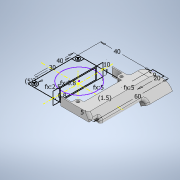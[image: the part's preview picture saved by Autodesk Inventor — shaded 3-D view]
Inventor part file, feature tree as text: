
AUTODESK INVENTOR PART (.ipt)
format: ipt  version: 2020.2 (Build 242310000, 310)  size: 784,384 bytes
history: native  units: mm
features: extrude x16, sketch x6, draft x6, thicken_offset x5, plane x4, fillet x3, projected_geometry x3, shell x1
ambient origin geometry x8: Origin, YZ Plane, XZ Plane, XY Plane, X Axis, Y Axis, Z Axis, Center Point
bodies: Solid1 (feature_tree), Solid3 (feature_tree)
feature tree (44):
  sketch  "Sketch2"  dims[d0=40.0mm d1=40.0mm]
  sketch  "Sketch15"  dims[d6=10.0mm d7=5.0mm]
  plane  "Work Plane1"
  sketch  "Sketch3"  dims[d2=2.5mm d3=30.0mm]
  sketch  "Sketch5"  dims[d4=5.0mm d5=3.0mm]
  plane  "Work Plane2"
  extrude  "Extrusion1"  Depth=40.0mm
  extrude  "Extrusion2"  Depth=30.0mm
  extrude  "Extrusion12"  Depth=3.0mm
  extrude  "Extrusion3"  Depth=10.0mm
  extrude  "Extrusion4"  TaperAngle=0.0deg  [1 undecoded]
  extrude  "Extrusion10"  Depth=10.0mm TaperAngle=0.0deg
  extrude  "Extrusion5"  Depth=10.0mm
  plane  "Work Plane4"
  plane  "Work Plane7"
  extrude  "Extrusion28"  TaperAngle=0.0deg  [1 undecoded]
  extrude  "Extrusion29"  Depth=10.0mm
  draft  "FaceDraft20"
  draft  "FaceDraft21"
  draft  "FaceDraft22"
  draft  "FaceDraft23"
  extrude  "Extrusion31"  Depth=10.0mm
  draft  "FaceDraft29"
  fillet  "Fillet28"  Radius=20.0mm
  shell  "Shell4"  Thickness=0.0mm
  extrude  "Extrusion33"  Depth=10.0mm
  extrude  "Extrusion34"  Depth=10.0mm
  extrude  "Extrusion39"  TaperAngle=0.0deg  [1 undecoded]
  extrude  "Extrusion35"  Depth=10.0mm
  draft  "FaceDraft30"
  extrude  "Extrusion37"  Depth=10.0mm
  extrude  "Extrusion36"  [1 undecoded]
  thicken_offset  "Thicken16"
  thicken_offset  "Thicken20"
  thicken_offset  "Thicken17"
  fillet  "Fillet26"  Radius=20.0mm
  fillet  "Fillet22"  Radius=0.5mm
  thicken_offset  "Thicken18"
  thicken_offset  "Thicken19"
  sketch  "Sketch18"  dims[d8=1.4mm d9=0.0mm]
  projected_geometry  "Projected Loop4"
  sketch  "Sketch19"  dims[d10=0.0mm d11=1.4mm d12=0.0mm d13=5.0mm d14=0.0mm d15=0.8mm d16=0.8mm d17=20.0mm d18=0.0mm d19=20.0mm d25=5.0mm d26=0.0mm d28=1.5mm d36=60.0mm d44=-5.0mm d69=20.0mm d71=0.5mm d72=0.0mm d76=5.0mm d77=0.0mm d112=9.0mm d121=12.0mm d122=0.0mm d126=-12.0mm d168=5.0mm d188=30.0deg d198=15.0mm d210=5.0mm d211=5.0mm d212=0.0mm d213=11.0mm d214=0.0mm d217=30.0deg d218=30.0deg d225=0.8mm d226=30.0deg d227=30.0deg d228=5.0mm d229=10.0mm d230=0.0mm d239=30.0deg d241=0.0mm d242=0.0mm d243=10.0mm d244=0.0mm d245=30.936mm d246=0.0mm d247=10.0mm d248=0.0mm d249=30.0deg d250=2.0mm d252=10.0mm d253=0.0mm d254=8.0mm d255=1.0mm d256=0.0mm d260=0.0mm d261=0.0mm d265=1.0mm d266=0.0mm d267=8.0mm d268=0.0mm d284=0.4mm d286=2.0mm d298=12.0mm d300=0.12mm d301=0.1mm d302=0.12mm d303=0.1mm d304=0.4mm d305=0.5mm d306=0.4mm d307=0.4mm d308=0.12mm d309=0.4mm d123=0.5mm d124=0.872665mm d125=0.5mm d150=0.5mm d151=0.872665mm d152=0.5mm d153=0.872665mm d189=0.872665mm d190=0.5mm d191=0.872665mm d269=0.5mm d270=0.872665mm d271=0.5mm d272=0.872665mm]
  projected_geometry  "Projected Loop5"
  projected_geometry  "Projected Loop7"
note: 4 required parameter values undecoded (feature->parameter linkage not recoverable at this tier; creation-order binding heuristic only, values carry confidence <= 0.55)
